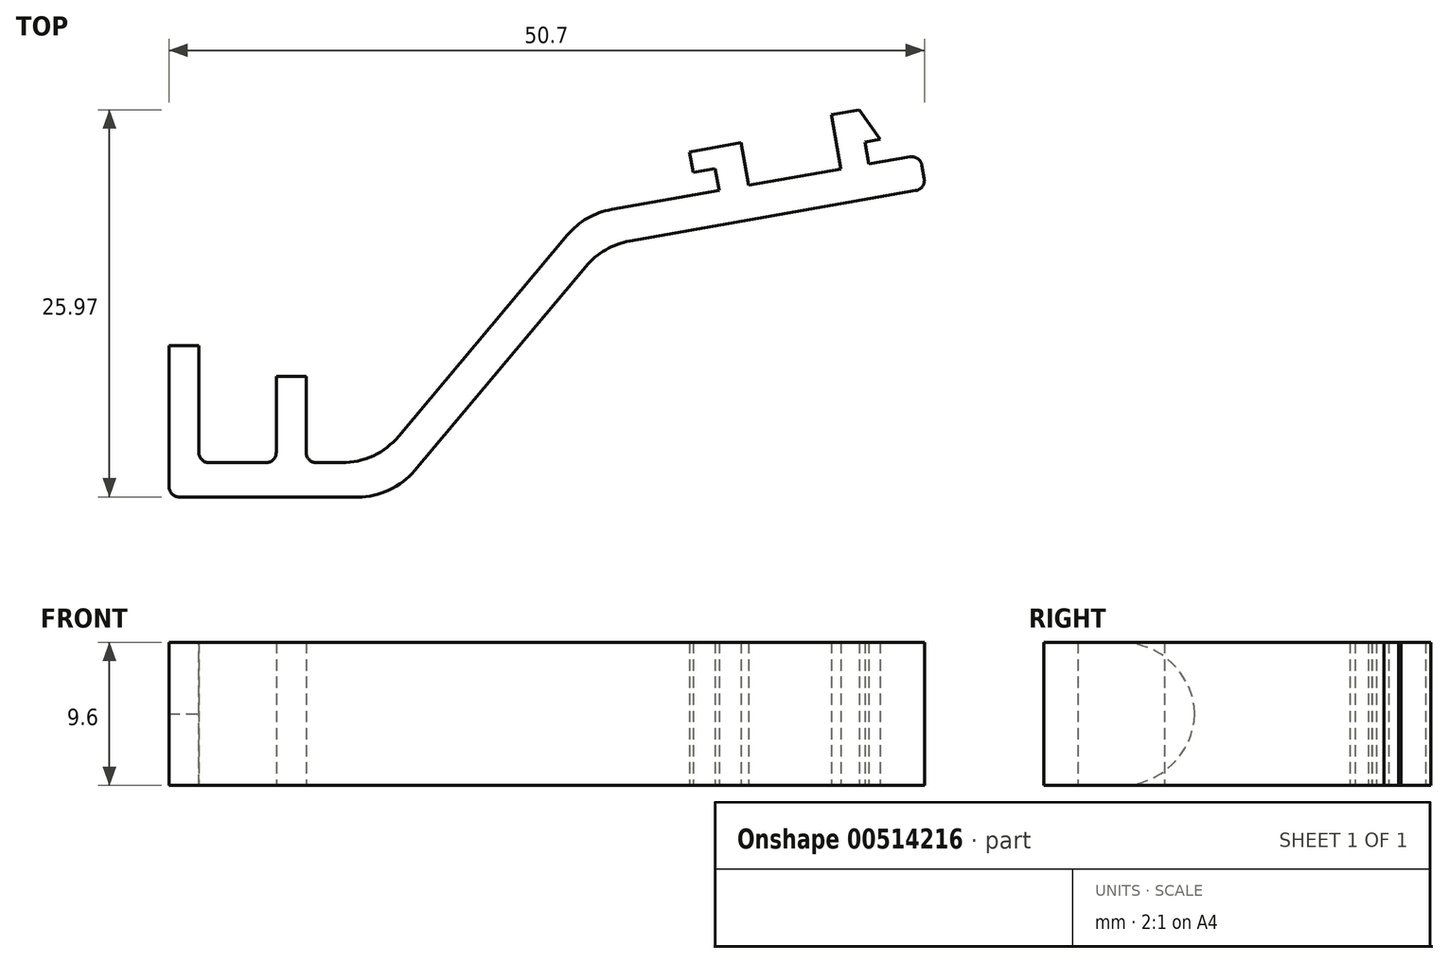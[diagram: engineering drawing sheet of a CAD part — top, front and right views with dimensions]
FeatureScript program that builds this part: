
annotation { "Feature Type Name" : "Feature", "Feature Type Description" : "" }
export const myFeature = defineFeature(function(context is Context, id is Id, definition is map)
    precondition{}
    {
        {
            var Q0;
            Q0=qCreatedBy(makeId("Top.planeOp"),FACE);
            var sketch = newSketch(context, id + "F0", { "sketchPlane" : qUnion([Q0])});
            skLineSegment(sketch, "E0", {"start": v(0, 0) * mm, "end": v(-15, 0) * mm});
            skLineSegment(sketch, "E1", {"start": v(0, 0) * mm, "end": v(14.14, 16.85) * mm});
            skLineSegment(sketch, "E2", {"start": v(14.14, 16.85) * mm, "end": v(35.8, 20.67) * mm});
            skLineSegment(sketch, "E3.0", {"start": v(12.92, 18.97) * mm, "end": v(35.4, 22.94) * mm});
            skLineSegment(sketch, "E3.1", {"start": v(-1.07, 2.3) * mm, "end": v(12.92, 18.97) * mm});
            skLineSegment(sketch, "E3.2", {"start": v(-1.07, 2.3) * mm, "end": v(-15, 2.3) * mm});
            skLineSegment(sketch, "E4", {"start": v(-15, 0) * mm, "end": v(-15, 2.3) * mm});
            skLineSegment(sketch, "E5", {"start": v(35.8, 20.67) * mm, "end": v(35.4, 22.94) * mm});
            skLineSegment(sketch, "E6", {"start": v(-15, 2.3) * mm, "end": v(-15, 10.15) * mm});
            skLineSegment(sketch, "E7", {"start": v(-15, 10.15) * mm, "end": v(-13, 10.15) * mm});
            skLineSegment(sketch, "E8", {"start": v(-13, 10.15) * mm, "end": v(-13, 2.3) * mm});
            skLineSegment(sketch, "E9", {"start": v(-7.8, 2.3) * mm, "end": v(-7.8, 8.1) * mm});
            skLineSegment(sketch, "E10", {"start": v(-7.8, 8.1) * mm, "end": v(-5.8, 8.1) * mm});
            skLineSegment(sketch, "E11", {"start": v(-5.8, 8.1) * mm, "end": v(-5.8, 2.3) * mm});
            skLineSegment(sketch, "E12", {"start": v(31.96, 22.33) * mm, "end": v(31.32, 25.97) * mm});
            skLineSegment(sketch, "E13", {"start": v(31.32, 25.97) * mm, "end": v(29.45, 25.64) * mm});
            skLineSegment(sketch, "E14", {"start": v(29.45, 25.64) * mm, "end": v(30.09, 22) * mm});
            skLineSegment(sketch, "E15", {"start": v(21.92, 20.56) * mm, "end": v(21.41, 23.42) * mm});
            skLineSegment(sketch, "E16", {"start": v(23.38, 23.76) * mm, "end": v(21.41, 23.42) * mm});
            skLineSegment(sketch, "E17", {"start": v(23.38, 23.76) * mm, "end": v(23.89, 20.9) * mm});
            skLineSegment(sketch, "E18", {"start": v(31.32, 25.97) * mm, "end": v(32.72, 23.99) * mm});
            skLineSegment(sketch, "E19", {"start": v(32.72, 23.99) * mm, "end": v(31.64, 23.8) * mm});
            skPoint(sketch, "E19.endSnap0", {"position": v(31.64, 24.15) * mm});
            skLineSegment(sketch, "E20", {"start": v(21.41, 23.42) * mm, "end": v(19.94, 23.15) * mm});
            skLineSegment(sketch, "E21", {"start": v(19.94, 23.15) * mm, "end": v(20.18, 21.78) * mm});
            skLineSegment(sketch, "E22", {"start": v(20.18, 21.78) * mm, "end": v(21.66, 22.04) * mm});
            skSolve(sketch);
        }
        {
            var Q0;
            Q0 = qSketchRegion(id + "F0", true);
            extrude(context, id + "F1", {"entities" : qUnion([Q0]), "depth" : 9.6 * mm});
        }
        {
            var Q0;
            Q0=makeQuery(id+"F1.opExtrude","CAP_EDGE",EDGE,{"disambiguationData":[OSD([sQuery(id+"F0.wireOp",EDGE,"E7")])],"isStart":false});
            var Q1;
            Q1=makeQuery(id+"F1.opExtrude","CAP_EDGE",EDGE,{"disambiguationData":[OSD([sQuery(id+"F0.wireOp",EDGE,"E7")])],"isStart":true});
            fillet(context, id + "F2", {"entities" : qUnion([Q0, Q1]), "radius" : 5 * mm, "tangentPropagation" : true, "allowEdgeOverflow" : false});
        }
        {
            var Q0;
            Q0=makeQuery(id+"F1.opExtrude","SWEPT_EDGE",EDGE,{"disambiguationData":[OSD([sQuery(id+"F0.wireOp",EDGE,"E3.2"),sQuery(id+"F0.wireOp",EDGE,"E8")])]});
            var Q1;
            Q1=makeQuery(id+"F1.opExtrude","SWEPT_EDGE",EDGE,{"disambiguationData":[OSD([sQuery(id+"F0.wireOp",EDGE,"E3.2"),sQuery(id+"F0.wireOp",EDGE,"E9")])]});
            var Q2;
            Q2=makeQuery(id+"F1.opExtrude","SWEPT_EDGE",EDGE,{"disambiguationData":[OSD([sQuery(id+"F0.wireOp",EDGE,"E3.2"),sQuery(id+"F0.wireOp",EDGE,"E11")])]});
            var Q3;
            Q3=makeQuery(id+"F1.opExtrude","SWEPT_EDGE",EDGE,{"disambiguationData":[OSD([sQuery(id+"F0.wireOp",EDGE,"E0"),sQuery(id+"F0.wireOp",EDGE,"E4")])]});
            var Q4;
            Q4=makeQuery(id+"F1.opExtrude","SWEPT_EDGE",EDGE,{"disambiguationData":[OSD([sQuery(id+"F0.wireOp",EDGE,"E3.0"),sQuery(id+"F0.wireOp",EDGE,"E5")])]});
            var Q5;
            Q5=makeQuery(id+"F1.opExtrude","SWEPT_EDGE",EDGE,{"disambiguationData":[OSD([sQuery(id+"F0.wireOp",EDGE,"E2"),sQuery(id+"F0.wireOp",EDGE,"E5")])]});
            fillet(context, id + "F3", {"entities" : qUnion([Q0, Q1, Q2, Q3, Q4, Q5]), "radius" : 0.7 * mm, "tangentPropagation" : true, "allowEdgeOverflow" : false});
        }
        {
            var Q0;
            Q0=makeQuery(id+"F1.opExtrude","SWEPT_EDGE",EDGE,{"disambiguationData":[OSD([sQuery(id+"F0.wireOp",EDGE,"E0"),sQuery(id+"F0.wireOp",EDGE,"E1")])]});
            var Q1;
            Q1=makeQuery(id+"F1.opExtrude","SWEPT_EDGE",EDGE,{"disambiguationData":[OSD([sQuery(id+"F0.wireOp",EDGE,"E3.0"),sQuery(id+"F0.wireOp",EDGE,"E3.1")])]});
            var Q2;
            Q2=makeQuery(id+"F1.opExtrude","SWEPT_EDGE",EDGE,{"disambiguationData":[OSD([sQuery(id+"F0.wireOp",EDGE,"E1"),sQuery(id+"F0.wireOp",EDGE,"E2")])]});
            var Q3;
            Q3=makeQuery(id+"F1.opExtrude","SWEPT_EDGE",EDGE,{"disambiguationData":[OSD([sQuery(id+"F0.wireOp",EDGE,"E3.1"),sQuery(id+"F0.wireOp",EDGE,"E3.2")])]});
            fillet(context, id + "F4", {"entities" : qUnion([Q0, Q1, Q2, Q3]), "radius" : 5 * mm, "tangentPropagation" : true, "allowEdgeOverflow" : false});
        }
    });
